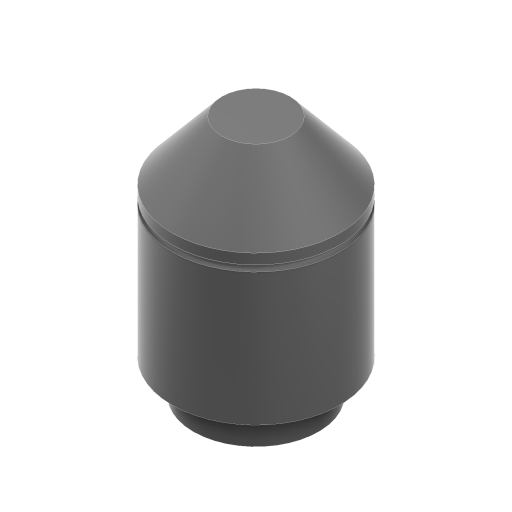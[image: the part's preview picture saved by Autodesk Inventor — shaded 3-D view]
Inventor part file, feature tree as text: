
AUTODESK INVENTOR PART (.ipt)
format: ipt  version: 2024.1 (Build 281209000, 209)  size: 151,040 bytes
history: native  units: mm
features: revolve x1, sketch x1
ambient origin geometry x8: Origin, YZ Plane, XZ Plane, XY Plane, X Axis, Y Axis, Z Axis, Center Point
bodies: Volumenkörper1 (feature_tree)
feature tree (2):
  revolve  "Umdrehung1"
  sketch  "Skizze1"  dims[d0=24.0mm d1=24.43461mm d2=5.5mm d3=1.0mm d4=0.5mm d5=1.65mm d6=0.5mm d7=12.225mm d8=4.93mm d9=10.08mm d10=90.0deg]
